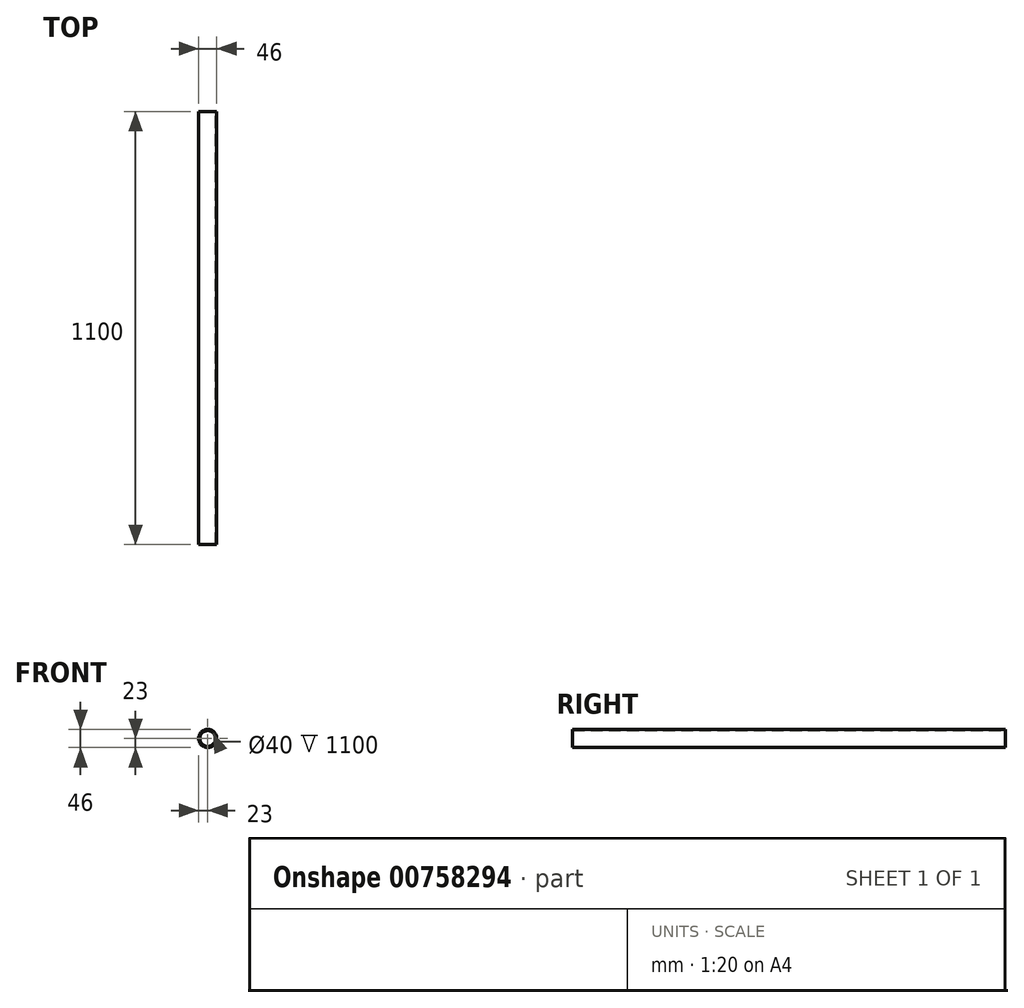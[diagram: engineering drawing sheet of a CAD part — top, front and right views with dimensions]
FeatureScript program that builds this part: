
annotation { "Feature Type Name" : "Feature", "Feature Type Description" : "" }
export const myFeature = defineFeature(function(context is Context, id is Id, definition is map)
    precondition{}
    {
        {
            var Q0;
            Q0=qCreatedBy(makeId("Front.planeOp"),FACE);
            var sketch = newSketch(context, id + "F0", { "sketchPlane" : qUnion([Q0])});
            skCircle(sketch, "E0", {"center": v(0, 0) * mm, "radius": 20 * mm});
            skCircle(sketch, "E1", {"center": v(0, 0) * mm, "radius": 23 * mm});
            skSolve(sketch);
        }
        {
            var Q0;
            Q0 = qSketchRegion(id + "F0", true);
            extrude(context, id + "F1", {"entities" : qUnion([Q0]), "depth" : 1100 * mm, "offsetDistance" : 25 * mm});
        }
    });
